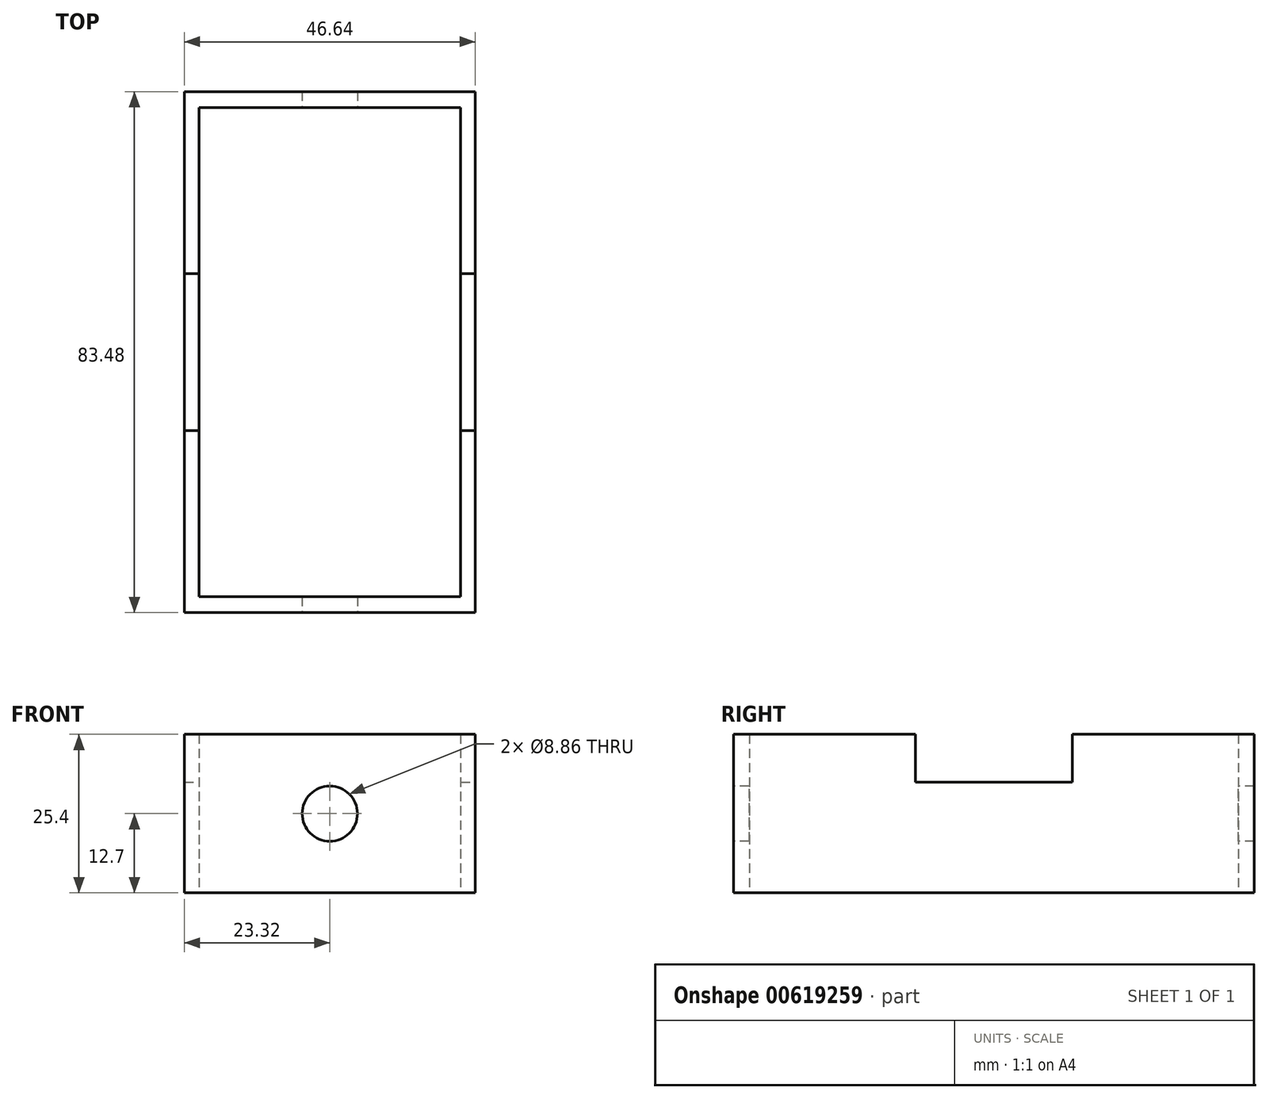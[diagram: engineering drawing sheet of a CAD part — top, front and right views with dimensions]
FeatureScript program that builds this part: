
annotation { "Feature Type Name" : "Feature", "Feature Type Description" : "" }
export const myFeature = defineFeature(function(context is Context, id is Id, definition is map)
    precondition{}
    {
        {
            var Q0;
            Q0=qCreatedBy(makeId("Top.planeOp"),FACE);
            var sketch = newSketch(context, id + "F0", { "sketchPlane" : qUnion([Q0])});
            skLineSegment(sketch, "E0.bottom", {"start": v(23.32, -41.74) * mm, "end": v(-23.32, -41.74) * mm});
            skLineSegment(sketch, "E0.top", {"start": v(23.32, 41.74) * mm, "end": v(-23.32, 41.74) * mm});
            skLineSegment(sketch, "E0.left", {"start": v(23.32, -41.74) * mm, "end": v(23.32, 41.74) * mm});
            skLineSegment(sketch, "E0.right", {"start": v(-23.32, -41.74) * mm, "end": v(-23.32, 41.74) * mm});
            skPoint(sketch, "E0.middle", {"position": v(0, 0) * mm});
            skLineSegment(sketch, "E1.bottom", {"start": v(20.98, -39.18) * mm, "end": v(-20.98, -39.18) * mm});
            skLineSegment(sketch, "E1.top", {"start": v(20.98, 39.18) * mm, "end": v(-20.98, 39.18) * mm});
            skLineSegment(sketch, "E1.left", {"start": v(20.98, -39.18) * mm, "end": v(20.98, 39.18) * mm});
            skLineSegment(sketch, "E1.right", {"start": v(-20.98, -39.18) * mm, "end": v(-20.98, 39.18) * mm});
            skSolve(sketch);
        }
        {
            var Q0;
            Q0=makeQuery(id+"F0.imprint","IMPRINT",FACE,{"disambiguationData":[TD([[makeQuery(id+"F0.imprint","IMPRINT",EDGE,{"derivedFrom":sQuery(id+"F0.wireOp",EDGE,"E0.bottom")}),-1.0]])]});
            extrude(context, id + "F1", {"entities" : qUnion([Q0]), "depth" : 25.4 * mm, "offsetDistance" : 25.4 * mm});
        }
        {
            var Q0;
            Q0=makeQuery(id+"F1.opExtrude","SWEPT_FACE",FACE,{"disambiguationData":[OSD([sQuery(id+"F0.wireOp",EDGE,"E0.left")])]});
            var sketch = newSketch(context, id + "F2", { "sketchPlane" : qUnion([Q0])});
            skLineSegment(sketch, "E2.bottom", {"start": v(-12.58, 17.75) * mm, "end": v(12.58, 17.75) * mm});
            skLineSegment(sketch, "E2.top", {"start": v(-12.58, 33.05) * mm, "end": v(12.58, 33.05) * mm});
            skLineSegment(sketch, "E2.left", {"start": v(-12.58, 17.75) * mm, "end": v(-12.58, 33.05) * mm});
            skLineSegment(sketch, "E2.right", {"start": v(12.58, 17.75) * mm, "end": v(12.58, 33.05) * mm});
            skPoint(sketch, "E2.middle", {"position": v(0, 25.4) * mm});
            skSolve(sketch);
        }
        {
            var Q0;
            {var subQ0=sQuery(id+"F2.wireOp",EDGE,"E2.bottom");Q0=makeQuery(id+"F2.imprint","IMPRINT",FACE,{"disambiguationData":[TD([[makeQuery(id+"F2.imprint","IMPRINT",EDGE,{"derivedFrom":subQ0}),1.0]])]});}
            extrude(context, id + "F3", {"entities" : qUnion([Q0]), "operationType" : NewBodyOperationType.REMOVE, "oppositeDirection" : true, "depth" : 76.2 * mm, "offsetDistance" : 25.4 * mm});
        }
        {
            var Q0;
            Q0=makeQuery(id+"F1.opExtrude","SWEPT_FACE",FACE,{"disambiguationData":[OSD([sQuery(id+"F0.wireOp",EDGE,"E0.bottom")])]});
            var sketch = newSketch(context, id + "F4", { "sketchPlane" : qUnion([Q0])});
            skLineSegment(sketch, "E3.left", {"start": v(0, 8.27) * mm, "end": v(0, 17.13) * mm});
            skPoint(sketch, "E3.middle", {"position": v(-23.32, 25.4) * mm});
            skCircle(sketch, "E4", {"center": v(0, 12.7) * mm, "radius": 4.43 * mm});
            skPoint(sketch, "E4.centerSnap0", {"position": v(-23.32, 12.7) * mm});
            skPoint(sketch, "E3.bottom.end.orphan", {"position": v(-46.63, -17.85) * mm});
            skPoint(sketch, "E5.orphan", {"position": v(0, -17.85) * mm});
            skPoint(sketch, "E3.top.end.orphan", {"position": v(-46.63, 68.65) * mm});
            skPoint(sketch, "E3.top.start.orphan", {"position": v(0, 68.65) * mm});
            skSolve(sketch);
        }
        {
            var Q0;
            {var subQ0=sQuery(id+"F4.wireOp",EDGE,"E3.left");Q0=makeQuery(id+"F4.imprint","IMPRINT",FACE,{"disambiguationData":[TD([[makeQuery(id+"F4.imprint","IMPRINT",EDGE,{"derivedFrom":subQ0}),-1.0]])]});}
            var Q1;
            {var subQ0=sQuery(id+"F4.wireOp",EDGE,"E3.left");Q1=makeQuery(id+"F4.imprint","IMPRINT",FACE,{"disambiguationData":[TD([[makeQuery(id+"F4.imprint","IMPRINT",EDGE,{"derivedFrom":subQ0}),1.0]])]});}
            extrude(context, id + "F5", {"entities" : qUnion([Q0, Q1]), "operationType" : NewBodyOperationType.REMOVE, "oppositeDirection" : true, "depth" : 127 * mm, "offsetDistance" : 25.4 * mm});
        }
    });
